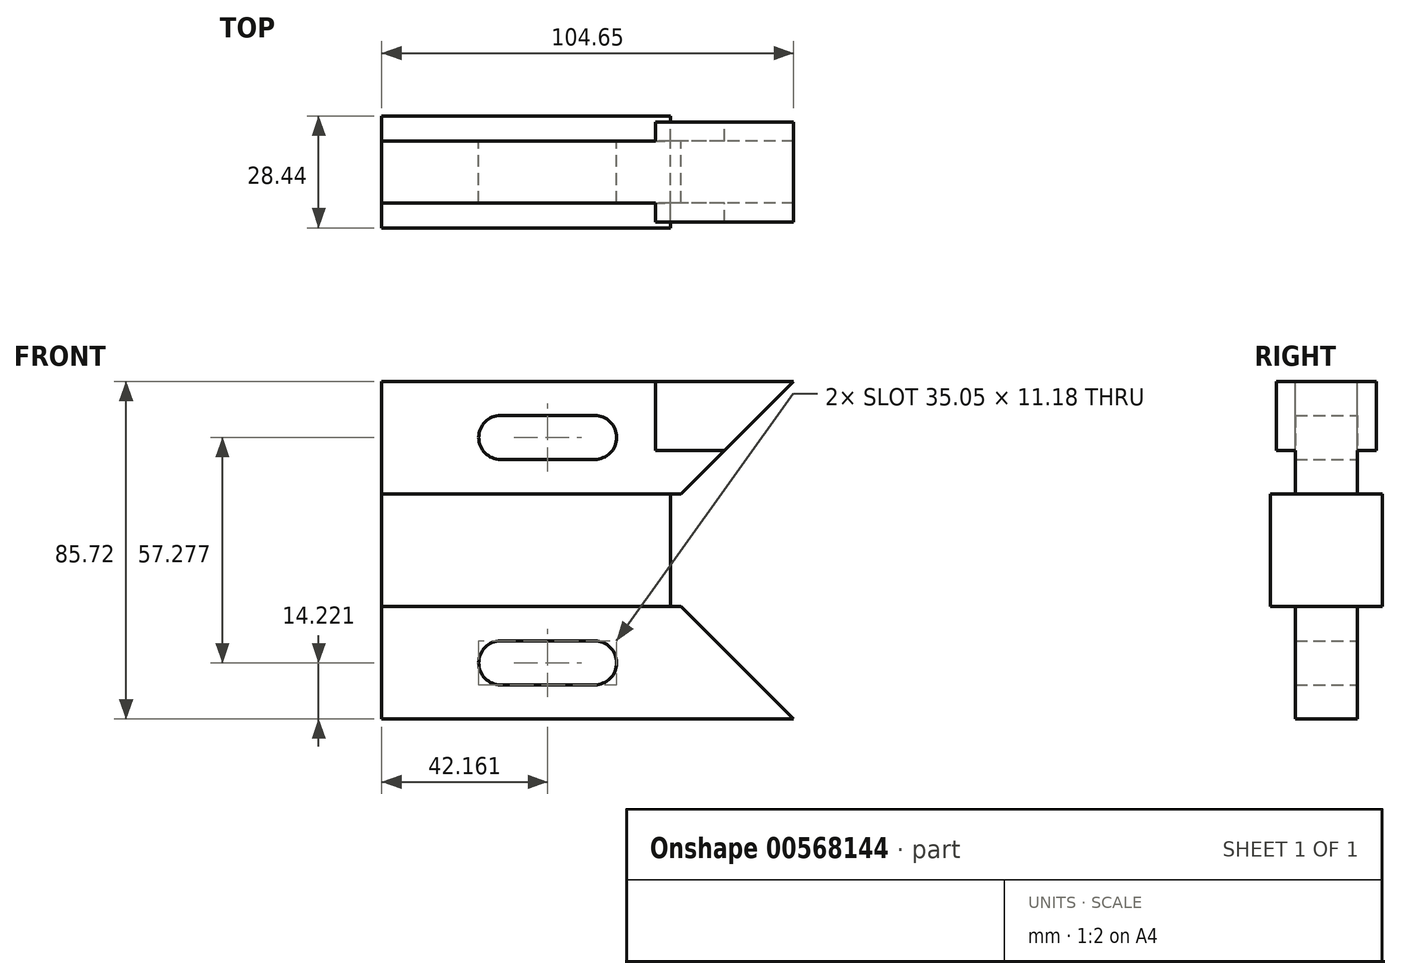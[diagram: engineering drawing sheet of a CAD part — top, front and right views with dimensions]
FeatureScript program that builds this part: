
annotation { "Feature Type Name" : "Feature", "Feature Type Description" : "" }
export const myFeature = defineFeature(function(context is Context, id is Id, definition is map)
    precondition{}
    {
        {
            var Q0;
            Q0=qCreatedBy(makeId("Front.planeOp"),FACE);
            var sketch = newSketch(context, id + "F0", { "sketchPlane" : qUnion([Q0])});
            skLineSegment(sketch, "E0.bottom", {"start": v(36.7, -14.29) * mm, "end": v(-36.7, -14.29) * mm});
            skLineSegment(sketch, "E0.top", {"start": v(36.7, 14.29) * mm, "end": v(-36.7, 14.29) * mm});
            skLineSegment(sketch, "E0.left", {"start": v(36.7, -14.29) * mm, "end": v(36.7, 14.29) * mm});
            skLineSegment(sketch, "E0.right", {"start": v(-36.7, -14.29) * mm, "end": v(-36.7, 14.29) * mm});
            skPoint(sketch, "E0.middle", {"position": v(0, 0) * mm});
            skSolve(sketch);
        }
        {
            var Q0;
            Q0=qCreatedBy(makeId("Front.planeOp"),FACE);
            var sketch = newSketch(context, id + "F1", { "sketchPlane" : qUnion([Q0])});
            skSolve(sketch);
        }
        {
            var Q0;
            Q0 = qSketchRegion(id + "F0", true);
            var Q1;
            Q1 = qSketchRegion(id + "F1", true);
            var Q2;
            Q2 = qSketchRegion(id + "F3", true);
            extrude(context, id + "F2", {"entities" : qUnion([Q0, Q1, Q2]), "endBound" : BoundingType.SYMMETRIC, "depth" : 28.45 * mm, "offsetDistance" : 25.4 * mm});
        }
        {
            var Q0;
            Q0=qCreatedBy(makeId("Front.planeOp"),FACE);
            var sketch = newSketch(context, id + "F3", { "sketchPlane" : qUnion([Q0])});
            skLineSegment(sketch, "E1.0", {"start": v(36.7, 14.29) * mm, "end": v(-36.7, 14.29) * mm});
            skLineSegment(sketch, "E2", {"start": v(-36.7, 14.29) * mm, "end": v(-36.7, 42.86) * mm});
            skLineSegment(sketch, "E3", {"start": v(-36.7, 42.86) * mm, "end": v(67.95, 42.86) * mm});
            skLineSegment(sketch, "E4", {"start": v(67.95, 42.86) * mm, "end": v(39.37, 14.29) * mm});
            skLineSegment(sketch, "E5", {"start": v(-36.7, 14.29) * mm, "end": v(39.37, 14.29) * mm});
            skCircle(sketch, "E6", {"center": v(-6.48, 28.64) * mm, "radius": 5.59 * mm});
            skCircle(sketch, "E7", {"center": v(17.4, 28.64) * mm, "radius": 5.59 * mm});
            skLineSegment(sketch, "E8", {"start": v(-6.48, 34.23) * mm, "end": v(17.4, 34.23) * mm});
            skLineSegment(sketch, "E9", {"start": v(17.4, 23.05) * mm, "end": v(-6.48, 23.05) * mm});
            skLineSegment(sketch, "E10.MirrorCS", {"start": v(-36.7, -42.86) * mm, "end": v(67.95, -42.86) * mm});
            skLineSegment(sketch, "E11.MirrorCS", {"start": v(67.95, -42.86) * mm, "end": v(39.37, -14.29) * mm});
            skLineSegment(sketch, "E12.MirrorCS", {"start": v(-36.7, -14.29) * mm, "end": v(39.37, -14.29) * mm});
            skLineSegment(sketch, "E13.MirrorCS", {"start": v(-36.7, -14.29) * mm, "end": v(-36.7, -42.86) * mm});
            skLineSegment(sketch, "E14.MirrorCS", {"start": v(17.4, -23.05) * mm, "end": v(-6.48, -23.05) * mm});
            skLineSegment(sketch, "E15.MirrorCS", {"start": v(-6.48, -34.23) * mm, "end": v(17.4, -34.23) * mm});
            skCircle(sketch, "E16.MirrorC", {"center": v(17.4, -28.64) * mm, "radius": 5.59 * mm});
            skCircle(sketch, "E17.MirrorC", {"center": v(-6.48, -28.64) * mm, "radius": 5.59 * mm});
            skLineSegment(sketch, "E18", {"start": v(32.9, 42.86) * mm, "end": v(32.9, 25.34) * mm});
            skLineSegment(sketch, "E19", {"start": v(32.9, 25.34) * mm, "end": v(50.42, 25.34) * mm});
            skSolve(sketch);
        }
        {
            var Q0;
            Q0=makeQuery(id+"F3.imprint","IMPRINT",FACE,{"disambiguationData":[TD([[makeQuery(id+"F3.imprint","IMPRINT",EDGE,{"derivedFrom":sQuery(id+"F3.wireOp",EDGE,"E10.MirrorCS")}),1.0]])]});
            var Q1;
            {var subQ1=sQuery(id+"F3.wireOp",EDGE,"E2");Q1=makeQuery(id+"F3.imprint","IMPRINT",FACE,{"disambiguationData":[TD([[makeQuery(id+"F3.imprint","IMPRINT",EDGE,{"derivedFrom":subQ1}),-1.0]])]});}
            var Q2;
            {var subQ3=sQuery(id+"F3.wireOp",EDGE,"E18");Q2=makeQuery(id+"F3.imprint","IMPRINT",FACE,{"disambiguationData":[TD([[makeQuery(id+"F3.imprint","IMPRINT",EDGE,{"derivedFrom":subQ3}),1.0]])]});}
            extrude(context, id + "F4", {"entities" : qUnion([Q0, Q1, Q2]), "operationType" : NewBodyOperationType.ADD, "endBound" : BoundingType.SYMMETRIC, "depth" : 15.75 * mm, "offsetDistance" : 25.4 * mm});
        }
        {
            var Q0;
            {var subQ3=sQuery(id+"F3.wireOp",EDGE,"E18");Q0=makeQuery(id+"F3.imprint","IMPRINT",FACE,{"disambiguationData":[TD([[makeQuery(id+"F3.imprint","IMPRINT",EDGE,{"derivedFrom":subQ3}),1.0]])]});}
            extrude(context, id + "F5", {"entities" : qUnion([Q0]), "operationType" : NewBodyOperationType.ADD, "endBound" : BoundingType.SYMMETRIC, "depth" : 25.4 * mm, "offsetDistance" : 25.4 * mm});
        }
    });
